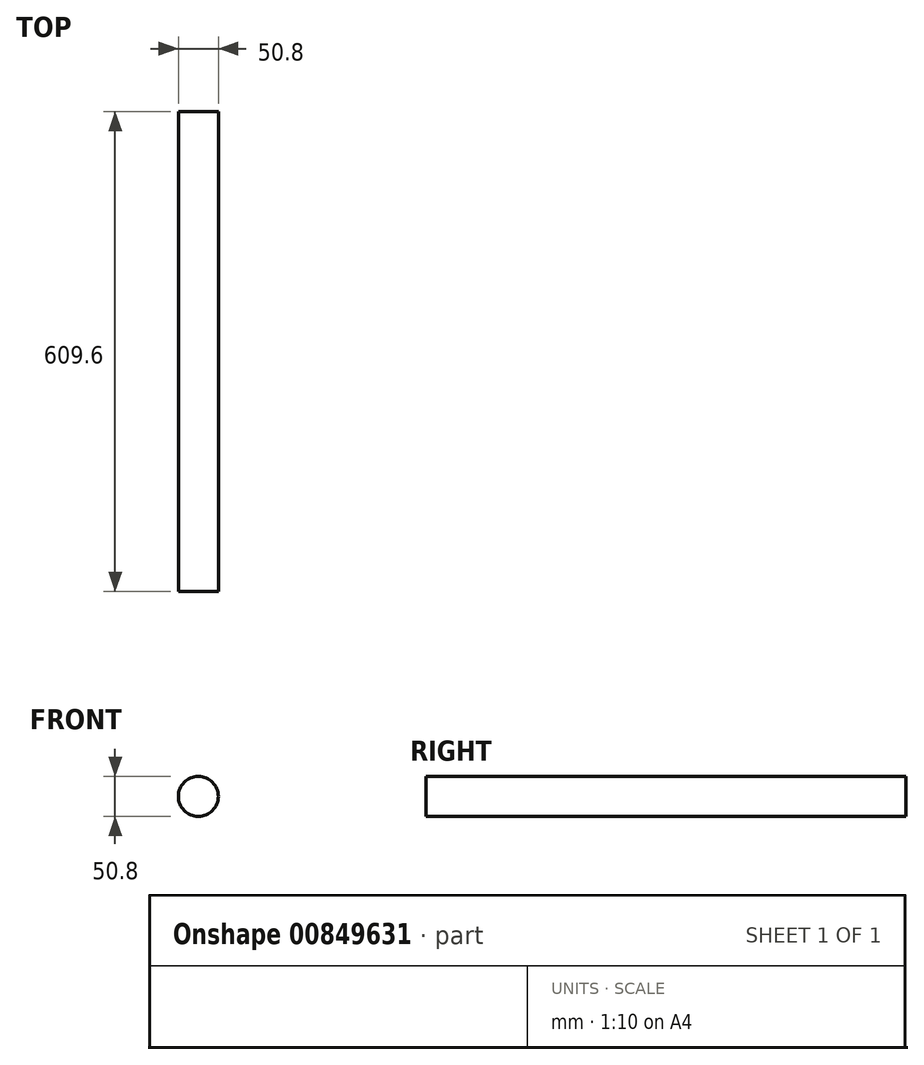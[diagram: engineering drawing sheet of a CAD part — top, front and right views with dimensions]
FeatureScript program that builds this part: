
annotation { "Feature Type Name" : "Feature", "Feature Type Description" : "" }
export const myFeature = defineFeature(function(context is Context, id is Id, definition is map)
    precondition{}
    {
        {
            var Q0;
            Q0=qCreatedBy(makeId("Front.planeOp"),FACE);
            var sketch = newSketch(context, id + "F0", { "sketchPlane" : qUnion([Q0])});
            skCircle(sketch, "E0", {"center": v(0, 0) * mm, "radius": 28.8 * mm});
            skCircle(sketch, "E1", {"center": v(0, 0) * mm, "radius": 25.4 * mm});
            skSolve(sketch);
        }
        {
            var Q0;
            Q0=makeQuery(id+"F0.imprint","IMPRINT",FACE,{"disambiguationData":[TD([[makeQuery(id+"F0.imprint","IMPRINT",EDGE,{"derivedFrom":sQuery(id+"F0.wireOp",EDGE,"E1")}),1.0]])]});
            extrude(context, id + "F1", {"entities" : qUnion([Q0]), "depth" : 609.6 * mm, "offsetDistance" : 25.4 * mm});
        }
    });
